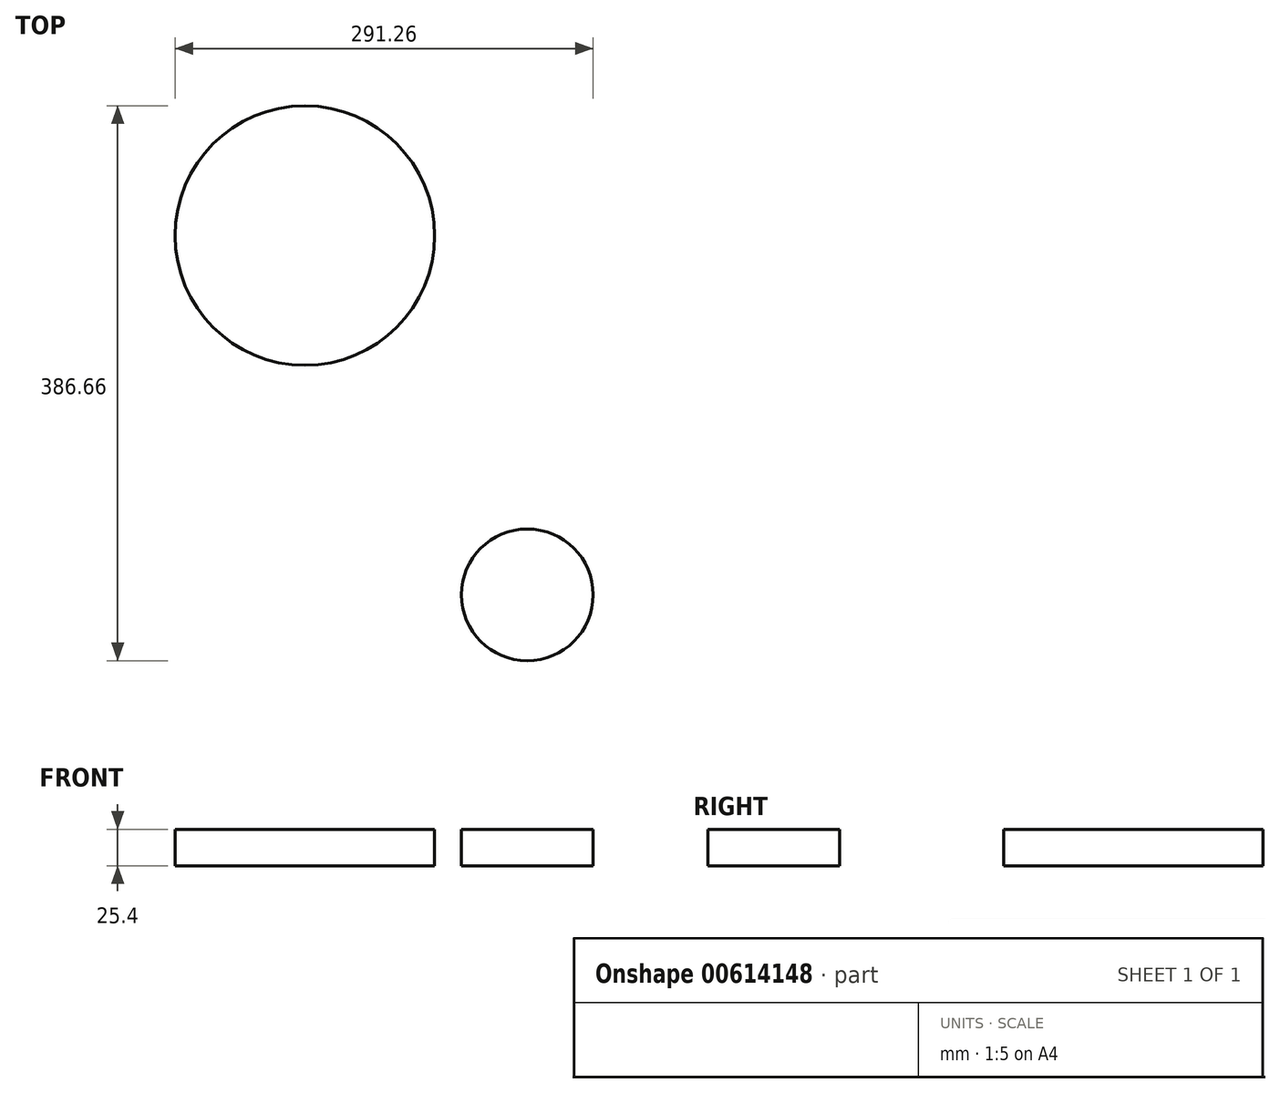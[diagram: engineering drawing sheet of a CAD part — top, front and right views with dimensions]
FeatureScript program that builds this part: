
annotation { "Feature Type Name" : "Feature", "Feature Type Description" : "" }
export const myFeature = defineFeature(function(context is Context, id is Id, definition is map)
    precondition{}
    {
        {
            var Q0;
            Q0=qCreatedBy(makeId("Top.planeOp"),FACE);
            var sketch = newSketch(context, id + "F0", { "sketchPlane" : qUnion([Q0])});
            skCircle(sketch, "E0", {"center": v(-32.72, 57.75) * mm, "radius": 90.4 * mm});
            skPoint(sketch, "E0.first.point", {"position": v(51.4, 90.87) * mm});
            skPoint(sketch, "E0.second.point", {"position": v(36.84, 0) * mm});
            skPoint(sketch, "E0.third.point", {"position": v(0, -26.53) * mm});
            skCircle(sketch, "E1", {"center": v(122.22, -192.6) * mm, "radius": 45.9 * mm});
            skPoint(sketch, "E1.first.point", {"position": v(82.92, -216.32) * mm});
            skPoint(sketch, "E1.second.point", {"position": v(145.86, -231.95) * mm});
            skPoint(sketch, "E1.third.point", {"position": v(96.55, -230.66) * mm});
            skCircle(sketch, "E2", {"center": v(161.9, -107.02) * mm, "radius": 135.92 * mm, "construction": true});
            skPoint(sketch, "E2.first.point", {"position": v(237.11, -220.23) * mm});
            skPoint(sketch, "E2.second.point", {"position": v(185.27, 26.88) * mm});
            skPoint(sketch, "E2.third.point", {"position": v(126.67, -238.29) * mm});
            skSolve(sketch);
        }
        {
            var Q0;
            Q0 = qSketchRegion(id + "F0", true);
            extrude(context, id + "F1", {"entities" : qUnion([Q0]), "depth" : 25.4 * mm, "offsetDistance" : 25.4 * mm});
        }
    });
